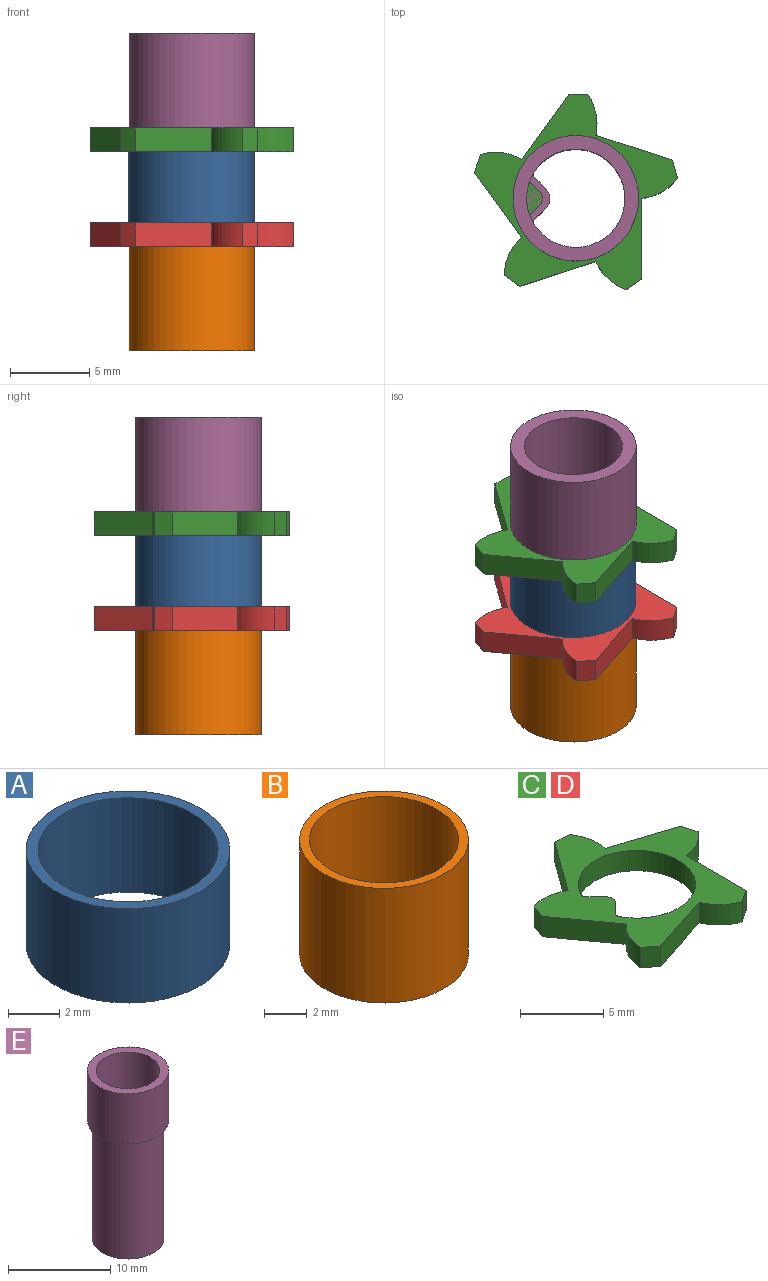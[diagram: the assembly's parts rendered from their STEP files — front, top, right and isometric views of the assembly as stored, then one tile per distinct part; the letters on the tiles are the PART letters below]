
ASSEMBLY  parts=5 mates=4
PART A: 4 faces, bbox 7.9x7.9x4.5 mm
  f0: cylinder r=3.51mm len=7.02mm, axis (0,0,-1), area 99.2mm2, adj f2,f3
  f1: cylinder r=3.97mm len=7.94mm, axis (0,0,-1), area 112.2mm2, adj f2,f3
  f2: plane 7.94x7.94mm, normal (0,0,1), area 10.8mm2, adj f0,f1
  f3: plane 7.94x7.94mm, normal (0,0,-1), area 10.8mm2, adj f0,f1
PART B: 4 faces, bbox 7.9x7.9x6.6 mm
  f0: cylinder r=3.51mm len=7.02mm, axis (0,0,-1), area 145.5mm2, adj f2,f3
  f1: cylinder r=3.97mm len=7.94mm, axis (0,0,-1), area 164.6mm2, adj f2,f3
  f2: plane 7.94x7.94mm, normal (0,0,1), area 10.8mm2, adj f0,f1
  f3: plane 7.94x7.94mm, normal (0,0,-1), area 10.8mm2, adj f0,f1
PART C: 23 faces, bbox 12.9x12.4x1.5 mm
  f0: plane 5.09x1.5mm, normal (1,0,0), area 7.6mm2, adj f1,f20,f21,f22
  f1: cylinder r=3.29mm len=2.28mm, axis (0,0,-1), area 4mm2, adj f0,f2,f21,f22
  f2: plane 1.5x1.15mm, normal (0.96,0.28,0), area 1.8mm2, adj f1,f3,f21,f22
  f3: plane 4.84x1.57mm, normal (0.31,0.95,0), area 7.6mm2, adj f2,f4,f21,f22
  f4: cylinder r=3.29mm len=2.56mm, axis (0,0,-1), area 4mm2, adj f3,f5,f21,f22
  f5: plane 1.5x1.2mm, normal (0.03,1,0), area 1.8mm2, adj f4,f6,f21,f22
  f6: plane 4.12x2.99mm, normal (-0.81,0.59,0), area 7.6mm2, adj f5,f7,f21,f22
  f7: cylinder r=3.29mm len=2.59mm, axis (0,0,-1), area 4mm2, adj f6,f8,f21,f22
  f8: plane 1.5x1.13mm, normal (-0.94,0.34,0), area 1.8mm2, adj f7,f9,f21,f22
  f9: plane 4.12x2.99mm, normal (-0.81,-0.59,0), area 7.6mm2, adj f8,f10,f21,f22
  f10: cylinder r=3.29mm len=2.37mm, axis (0,0,-1), area 4mm2, adj f9,f11,f21,f22
  f11: plane 1.5x0.95mm, normal (-0.61,-0.79,0), area 1.8mm2, adj f10,f12,f21,f22
  f12: plane 4.84x1.57mm, normal (0.31,-0.95,0), area 7.6mm2, adj f11,f13,f21,f22
  f13: cylinder r=3.29mm len=1.91mm, axis (0,0,-1), area 4mm2, adj f12,f20,f21,f22
  f14: cylinder r=3.53mm len=7.06mm, axis (0,0,-1), area 28.3mm2, adj f15,f19,f21,f22
  f15: cylinder r=0.3mm len=1.5mm, axis (0,0,-1), area 0.6mm2, adj f14,f16,f21,f22
  f16: plane 1.5x0.83mm, normal (0.71,-0.71,0), area 1.8mm2, adj f15,f17,f21,f22
  f17: cylinder r=0.6mm len=1.5mm, axis (0,0,-1), area 1.4mm2, adj f16,f18,f21,f22
  f18: plane 1.5x0.83mm, normal (0.71,0.71,0), area 1.8mm2, adj f17,f19,f21,f22
  f19: cylinder r=0.3mm len=1.5mm, axis (0,0,-1), area 0.6mm2, adj f14,f18,f21,f22
  f20: plane 1.5x0.99mm, normal (0.56,-0.83,0), area 1.8mm2, adj f0,f13,f21,f22
  f21: plane 12.87x12.36mm, normal (0,0,1), area 52.2mm2, adj f0,f1,f2,f3,f4,f5,f6,f7
  f22: plane 12.87x12.36mm, normal (0,0,-1), area 52.2mm2, adj f0,f1,f2,f3,f4,f5,f6,f7
PART D: same geometry as C
PART E: 12 faces, bbox 7.9x7.9x20.1 mm
  f0: cylinder r=3.11mm len=20.1mm, axis (0,0,-1), area 346.2mm2, adj f2,f4,f5,f9,f11
  f1: cylinder r=3.97mm len=7.94mm, axis (0,0,-1), area 149.7mm2, adj f2,f3
  f2: plane 7.94x7.94mm, normal (0,0,1), area 19.2mm2, adj f0,f1
  f3: plane 7.94x7.94mm, normal (0,0,-1), area 10.8mm2, adj f1,f10
  f4: plane 3.13x1.46mm, normal (0,0,1), area 2.7mm2, adj f0,f5,f6,f7,f8,f9
  f5: cylinder r=0.15mm len=14.1mm, axis (0,0,1), area 2.8mm2, adj f0,f4,f6,f11
  f6: plane 14.1x0.75mm, normal (0.71,0.71,0), area 14.9mm2, adj f4,f5,f7,f11
  f7: cylinder r=0.9mm len=14.1mm, axis (0,0,1), area 19.9mm2, adj f4,f6,f8,f11
  f8: plane 14.1x0.75mm, normal (0.71,-0.71,0), area 14.9mm2, adj f4,f7,f9,f11
  f9: cylinder r=0.15mm len=14.1mm, axis (0,0,1), area 2.8mm2, adj f0,f4,f8,f11
  f10: cylinder r=3.51mm len=14.1mm, axis (0,0,1), area 310.9mm2, adj f3,f11
  f11: plane 7.02x7.02mm, normal (0,0,-1), area 11mm2, adj f0,f5,f6,f7,f8,f9,f10
PLACE A t=(10.27,0,-6)mm
PLACE B t=(10.3,0,-14.1)mm
PLACE C t=(10.27,0,-1.5)mm
PLACE D t=(10.27,0,-7.5)mm
PLACE E t=(10.3,0,0)mm
MATE fastened C.f14 <-> A.f0  axis (0,0,-1) through (10.27,0,-1.5)mm
MATE fastened D.f14 <-> A.f0  axis (0,0,-1) through (10.27,0,-6)mm
MATE fastened B.f0 <-> E.f0  axis (0,0,-1) through (10.3,0,-14.1)mm
MATE fastened C.f21 <-> E.f0  axis (0,0,1) through (10.3,0,0)mm
